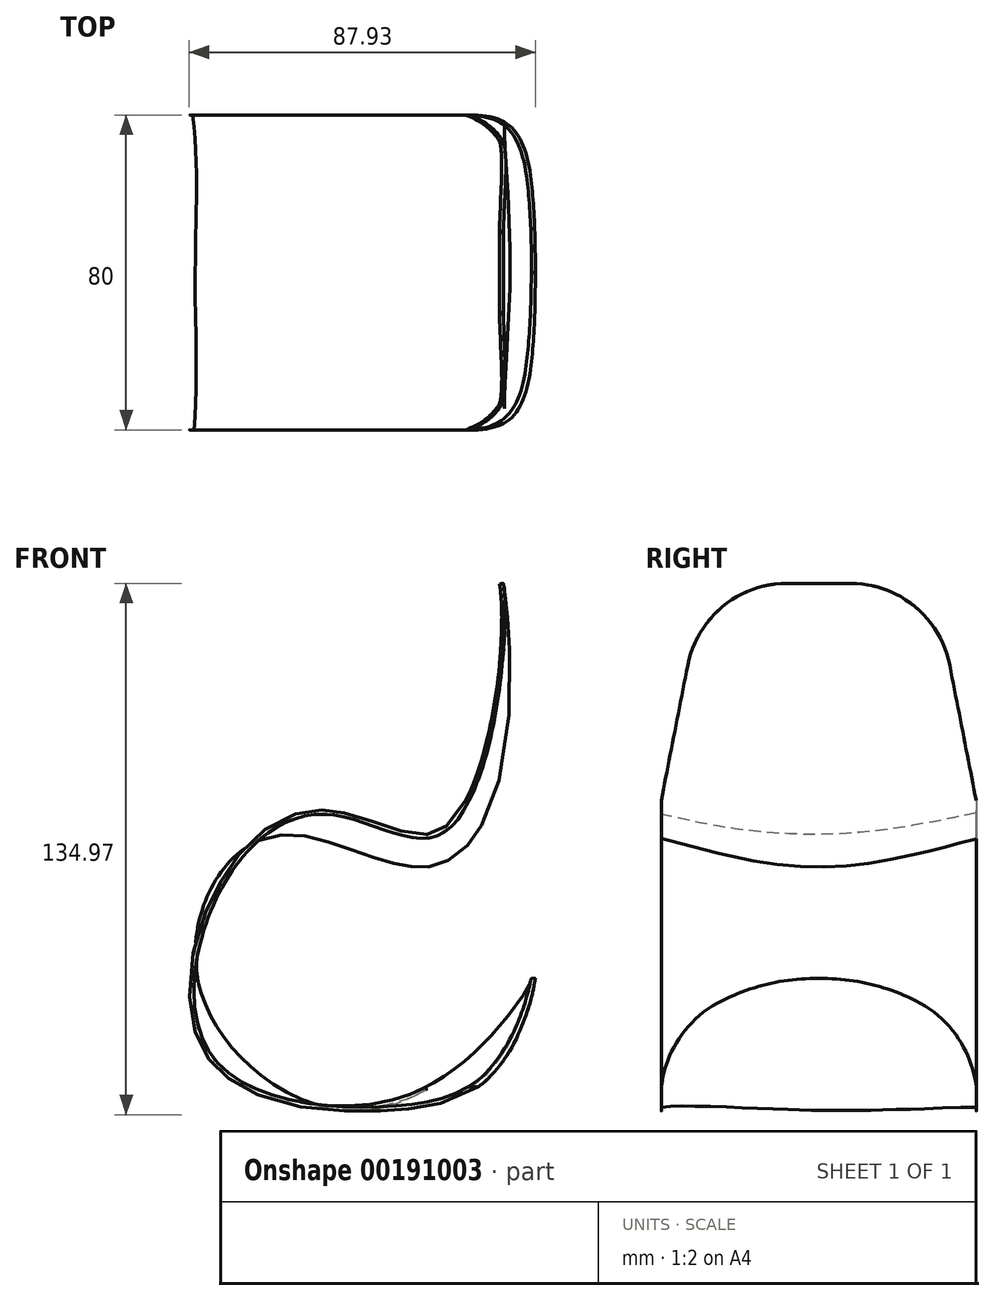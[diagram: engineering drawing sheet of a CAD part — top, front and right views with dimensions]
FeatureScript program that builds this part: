
annotation { "Feature Type Name" : "Feature", "Feature Type Description" : "" }
export const myFeature = defineFeature(function(context is Context, id is Id, definition is map)
    precondition{}
    {
        {
            var Q0;
            Q0=qCreatedBy(makeId("Front.planeOp"),FACE);
            cPlane(context, id + "F0", {"entities" : qUnion([Q0]), "cplaneType" : CPlaneType.OFFSET, "offset" : 40 * mm, "width" : 150 * mm, "height" : 150 * mm});
        }
        {
            var Q0;
            Q0=qCreatedBy(id+"F0.planeOp",FACE);
            var sketch = newSketch(context, id + "F1", { "sketchPlane" : qUnion([Q0])});
            skFitSpline(sketch, "E0", {"points": [v(44.76, 63.94) * mm, v(27.54, 0) * mm, v(0, 5.5) * mm, v(-26.55, -12.21) * mm, v(-29.21, -56.35) * mm, v(18.08, -68.48) * mm, v(50.82, -42.77) * mm], "startDerivative": vector(-17.73, -450.31) * mm, "endDerivative": vector(137.22, 364.15) * mm});
            skFitSpline(sketch, "E1.0", {"points": [v(43.76, 63.98) * mm, v(43.4, 54.62) * mm, v(42.39, 40.95) * mm, v(39.87, 25.25) * mm, v(37.32, 15.2) * mm, v(34.6, 8.64) * mm, v(32.1, 4.74) * mm, v(30.05, 2.54) * mm, v(28.24, 1.33) * mm, v(26.73, 0.75) * mm, v(25.12, 0.4) * mm, v(22.94, 0.35) * mm, v(20.06, 0.82) * mm, v(16.97, 1.69) * mm, v(13.73, 2.8) * mm, v(10.37, 4.02) * mm, v(6.93, 5.16) * mm, v(4.01, 5.93) * mm, v(1.67, 6.34) * mm, v(-0.1, 6.53) * mm, v(-1.86, 6.57) * mm, v(-4.18, 6.44) * mm, v(-7.03, 5.94) * mm, v(-10.35, 4.82) * mm, v(-14.61, 2.7) * mm, v(-18.59, -0.35) * mm, v(-22.21, -4.17) * mm, v(-24.74, -7.4) * mm, v(-27.06, -10.98) * mm, v(-29.16, -14.88) * mm, v(-31, -19.03) * mm, v(-33.08, -24.82) * mm, v(-34.87, -32.36) * mm, v(-35.35, -39.87) * mm, v(-34.78, -45.59) * mm, v(-33.84, -49.66) * mm, v(-32.33, -53.46) * mm, v(-30.57, -56.32) * mm, v(-28.85, -58.4) * mm, v(-26.93, -60.3) * mm, v(-24.2, -62.4) * mm, v(-20.47, -64.5) * mm, v(-15.02, -66.76) * mm, v(-7.48, -68.71) * mm, v(0.53, -69.66) * mm, v(6.92, -69.92) * mm, v(11.63, -69.9) * mm, v(15.43, -69.7) * mm, v(18.36, -69.47) * mm, v(21.2, -69.17) * mm, v(24.6, -68.68) * mm, v(29.73, -67.53) * mm, v(35.62, -65.24) * mm, v(41.84, -60.56) * mm, v(47.22, -53.53) * mm, v(50.31, -46.96) * mm, v(51.76, -43.12) * mm]});
            skLineSegment(sketch, "E2", {"start": v(43.76, 63.98) * mm, "end": v(44.76, 63.94) * mm});
            skLineSegment(sketch, "E3", {"start": v(50.82, -42.77) * mm, "end": v(51.76, -43.12) * mm});
            skSolve(sketch);
        }
        {
            var Q0;
            Q0=qCreatedBy(makeId("Front.planeOp"),FACE);
            var sketch = newSketch(context, id + "F2", { "sketchPlane" : qUnion([Q0])});
            skFitSpline(sketch, "E4", {"points": [v(44.43, 64.18) * mm, v(26.14, -7.7) * mm, v(-14.33, 0) * mm, v(-33.1, -36.83) * mm, v(12.22, -69.2) * mm, v(50.9, -38.12) * mm, v(51.56, -35.53) * mm], "startDerivative": vector(72.36, -532.06) * mm, "endDerivative": vector(-2.03, 40.07) * mm});
            skFitSpline(sketch, "E5.0", {"points": [v(43.44, 64.05) * mm, v(44.94, 53.01) * mm, v(45.68, 37.82) * mm, v(44, 21.13) * mm, v(41.53, 10.63) * mm, v(38.53, 3.74) * mm, v(35.65, -0.55) * mm, v(33.27, -3.13) * mm, v(30.7, -5.06) * mm, v(28.4, -6.12) * mm, v(26.45, -6.64) * mm, v(24.44, -6.94) * mm, v(21.76, -6.92) * mm, v(18.32, -6.37) * mm, v(13.5, -5.1) * mm, v(8.4, -3.27) * mm, v(3.2, -1.43) * mm, v(-0.73, -0.17) * mm, v(-4.65, 0.82) * mm, v(-7.9, 1.3) * mm, v(-10.45, 1.41) * mm, v(-12.35, 1.33) * mm, v(-14.23, 1.07) * mm, v(-16.07, 0.61) * mm, v(-17.86, -0.03) * mm, v(-20.16, -1.14) * mm, v(-22.87, -2.94) * mm, v(-25.82, -5.68) * mm, v(-29.3, -10) * mm, v(-32.7, -16.45) * mm, v(-34.55, -23.81) * mm, v(-34.93, -29.95) * mm, v(-34.67, -33.83) * mm, v(-34.13, -36.92) * mm, v(-33.38, -39.99) * mm, v(-32.03, -43.74) * mm, v(-29.84, -48.08) * mm, v(-26.23, -53.57) * mm, v(-20.56, -59.74) * mm, v(-13.73, -64.65) * mm, v(-7.8, -67.61) * mm, v(-3.16, -69.3) * mm, v(1.6, -70.37) * mm, v(6.45, -70.79) * mm, v(10.5, -70.54) * mm, v(13.7, -69.95) * mm, v(16.88, -69.11) * mm, v(20.76, -67.64) * mm, v(25.26, -65.31) * mm, v(29.54, -62.55) * mm, v(34.93, -58.44) * mm, v(39.75, -53.94) * mm, v(43.85, -49.5) * mm, v(46.51, -46.33) * mm, v(48.74, -43.43) * mm, v(50.19, -41.32) * mm, v(51.09, -39.88) * mm, v(51.63, -38.92) * mm, v(52.04, -38.1) * mm, v(52.31, -37.42) * mm, v(52.48, -36.81) * mm, v(52.56, -36.28) * mm, v(52.57, -35.82) * mm, v(52.56, -35.58) * mm, v(52.55, -35.48) * mm]});
            skLineSegment(sketch, "E6", {"start": v(43.44, 64.05) * mm, "end": v(44.43, 64.18) * mm});
            skLineSegment(sketch, "E7", {"start": v(51.56, -35.53) * mm, "end": v(52.55, -35.48) * mm});
            skSolve(sketch);
        }
        {
            var Q0;
            Q0=qCreatedBy(makeId("Front.planeOp"),FACE);
            cPlane(context, id + "F3", {"entities" : qUnion([Q0]), "cplaneType" : CPlaneType.OFFSET, "offset" : 40 * mm, "oppositeDirection" : true, "width" : 150 * mm, "height" : 150 * mm});
        }
        {
            var Q0;
            Q0=qCreatedBy(id+"F3.planeOp",FACE);
            var sketch = newSketch(context, id + "F4", { "sketchPlane" : qUnion([Q0])});
            skFitSpline(sketch, "E8.0", {"points": [v(43.76, 63.98) * mm, v(43.4, 54.62) * mm, v(42.39, 40.95) * mm, v(39.87, 25.25) * mm, v(37.32, 15.2) * mm, v(34.6, 8.64) * mm, v(32.1, 4.74) * mm, v(30.05, 2.54) * mm, v(28.24, 1.33) * mm, v(26.73, 0.75) * mm, v(25.12, 0.4) * mm, v(22.94, 0.35) * mm, v(20.06, 0.82) * mm, v(16.97, 1.69) * mm, v(13.73, 2.8) * mm, v(10.37, 4.02) * mm, v(6.93, 5.16) * mm, v(4.01, 5.93) * mm, v(1.67, 6.34) * mm, v(-0.1, 6.53) * mm, v(-1.86, 6.57) * mm, v(-4.18, 6.44) * mm, v(-7.03, 5.94) * mm, v(-10.35, 4.82) * mm, v(-14.61, 2.7) * mm, v(-18.59, -0.35) * mm, v(-22.21, -4.17) * mm, v(-24.74, -7.4) * mm, v(-27.06, -10.98) * mm, v(-29.16, -14.88) * mm, v(-31, -19.03) * mm, v(-33.08, -24.82) * mm, v(-34.87, -32.36) * mm, v(-35.35, -39.87) * mm, v(-34.78, -45.59) * mm, v(-33.84, -49.66) * mm, v(-32.33, -53.46) * mm, v(-30.57, -56.32) * mm, v(-28.85, -58.4) * mm, v(-26.93, -60.3) * mm, v(-24.2, -62.4) * mm, v(-20.47, -64.5) * mm, v(-15.02, -66.76) * mm, v(-7.48, -68.71) * mm, v(0.53, -69.66) * mm, v(6.92, -69.92) * mm, v(11.63, -69.9) * mm, v(15.43, -69.7) * mm, v(18.36, -69.47) * mm, v(21.2, -69.17) * mm, v(24.6, -68.68) * mm, v(29.73, -67.53) * mm, v(35.62, -65.24) * mm, v(41.84, -60.56) * mm, v(47.22, -53.53) * mm, v(50.31, -46.96) * mm, v(51.76, -43.12) * mm]});
            skFitSpline(sketch, "E9.0", {"points": [v(44.76, 63.94) * mm, v(44.57, 59.25) * mm, v(44.05, 50) * mm, v(42.75, 36.9) * mm, v(40.85, 25.06) * mm, v(38.7, 16.59) * mm, v(36.62, 10.88) * mm, v(34.86, 7.19) * mm, v(32.9, 4.14) * mm, v(30.72, 1.78) * mm, v(28.72, 0.45) * mm, v(27.01, -0.21) * mm, v(25.22, -0.6) * mm, v(22.85, -0.65) * mm, v(19.83, -0.16) * mm, v(16.67, 0.74) * mm, v(12.3, 2.24) * mm, v(6.64, 4.33) * mm, v(-0.2, 5.87) * mm, v(-6.83, 5.21) * mm, v(-13.1, 2.58) * mm, v(-17.92, -1.1) * mm, v(-21.45, -4.82) * mm, v(-23.92, -7.99) * mm, v(-26.2, -11.5) * mm, v(-28.26, -15.32) * mm, v(-30.07, -19.4) * mm, v(-32.12, -25.1) * mm, v(-33.88, -32.52) * mm, v(-34.43, -41.34) * mm, v(-33.14, -49.52) * mm, v(-29.72, -56.51) * mm, v(-23.87, -61.75) * mm, v(-16.2, -65.42) * mm, v(-7.3, -67.73) * mm, v(0.6, -68.66) * mm, v(6.94, -68.92) * mm, v(11.6, -68.9) * mm, v(15.37, -68.7) * mm, v(18.26, -68.47) * mm, v(21.07, -68.18) * mm, v(24.42, -67.7) * mm, v(28.18, -66.85) * mm, v(31.72, -65.68) * mm, v(36.13, -63.6) * mm, v(41.12, -59.86) * mm, v(46.34, -53.03) * mm, v(49.4, -46.56) * mm, v(50.82, -42.77) * mm]});
            skLineSegment(sketch, "E10", {"start": v(43.76, 63.98) * mm, "end": v(44.76, 63.94) * mm});
            skLineSegment(sketch, "E11", {"start": v(50.82, -42.77) * mm, "end": v(51.76, -43.12) * mm});
            skSolve(sketch);
        }
        {
            var Q0;
            Q0 = qSketchRegion(id + "F1", true);
            var Q1;
            Q1 = qSketchRegion(id + "F2", true);
            var Q2;
            Q2 = qSketchRegion(id + "F4", true);
            loft(context, id + "F5", {"sheetProfilesArray" : [{ "sheetProfileEntities" : qUnion([Q0]) }, { "sheetProfileEntities" : qUnion([Q1]) }, { "sheetProfileEntities" : qUnion([Q2]) }]});
        }
        {
            var Q0;
            Q0=qCreatedBy(makeId("Right.planeOp"),FACE);
            var sketch = newSketch(context, id + "F6", { "sketchPlane" : qUnion([Q0])});
            skLineSegment(sketch, "E12", {"start": v(33.28, 43.4) * mm, "end": v(40.27, 7.72) * mm});
            skLineSegment(sketch, "E13", {"start": v(40.27, 7.72) * mm, "end": v(50.1, 8.9) * mm});
            skLineSegment(sketch, "E14", {"start": v(50.1, 8.9) * mm, "end": v(47.4, 68.54) * mm});
            skLineSegment(sketch, "E15", {"start": v(47.4, 68.54) * mm, "end": v(0, 70.38) * mm});
            skLineSegment(sketch, "E16.MirrorCS", {"start": v(-47.4, 68.54) * mm, "end": v(0, 70.38) * mm});
            skLineSegment(sketch, "E17.MirrorCS", {"start": v(-50.1, 8.9) * mm, "end": v(-47.4, 68.54) * mm});
            skLineSegment(sketch, "E18.MirrorCS", {"start": v(-40.27, 7.72) * mm, "end": v(-50.1, 8.9) * mm});
            skLineSegment(sketch, "E19", {"start": v(0, 64.21) * mm, "end": v(8, 64.21) * mm});
            skArc(sketch, "E20", {"start": v(33.28, 43.4) * mm, "mid": v(24.37, 58.34) * mm, "end": v(8, 64.21) * mm});
            skLineSegment(sketch, "E21.MirrorCS", {"start": v(0, 64.21) * mm, "end": v(-8, 64.21) * mm});
            skArc(sketch, "E22.MirrorCS", {"start": v(-33.28, 43.4) * mm, "mid": v(-24.37, 58.34) * mm, "end": v(-8, 64.21) * mm});
            skLineSegment(sketch, "E23", {"start": v(-33.28, 43.4) * mm, "end": v(-40.27, 7.72) * mm});
            skSolve(sketch);
        }
        {
            var Q0;
            Q0 = qSketchRegion(id + "F6", true);
            extrude(context, id + "F7", {"entities" : qUnion([Q0]), "operationType" : NewBodyOperationType.REMOVE, "endBound" : BoundingType.THROUGH_ALL, "depth" : 25 * mm});
        }
        {
            var Q0;
            Q0=qCreatedBy(makeId("Right.planeOp"),FACE);
            var sketch = newSketch(context, id + "F8", { "sketchPlane" : qUnion([Q0])});
            skLineSegment(sketch, "E24", {"start": v(-63.09, -35.2) * mm, "end": v(51.03, -27.75) * mm});
            skLineSegment(sketch, "E25", {"start": v(51.03, -27.75) * mm, "end": v(51.41, -50.5) * mm});
            skArc(sketch, "E26", {"start": v(0, -36.2) * mm, "mid": v(-12.65, -37.53) * mm, "end": v(-24.63, -41.83) * mm});
            skArc(sketch, "E27", {"start": v(-24.63, -41.83) * mm, "mid": v(-38.84, -58.42) * mm, "end": v(-36.93, -80.18) * mm});
            skArc(sketch, "E28.MirrorCS", {"start": v(0, -36.2) * mm, "mid": v(12.65, -37.53) * mm, "end": v(24.63, -41.83) * mm});
            skArc(sketch, "E29.MirrorCS", {"start": v(24.63, -41.83) * mm, "mid": v(38.84, -58.42) * mm, "end": v(36.93, -80.18) * mm});
            skLineSegment(sketch, "E30", {"start": v(36.93, -80.18) * mm, "end": v(51.96, -77.05) * mm});
            skLineSegment(sketch, "E31", {"start": v(51.96, -77.05) * mm, "end": v(51.41, -50.5) * mm});
            skLineSegment(sketch, "E32", {"start": v(-63.09, -35.2) * mm, "end": v(-56.26, -72.15) * mm});
            skLineSegment(sketch, "E33", {"start": v(-56.26, -72.15) * mm, "end": v(-36.93, -80.18) * mm});
            skSolve(sketch);
        }
        {
            var Q0;
            Q0=makeQuery(id+"F8.imprint","IMPRINT",FACE,{"disambiguationData":[TD([[makeQuery(id+"F8.imprint","IMPRINT",EDGE,{"derivedFrom":sQuery(id+"F8.wireOp",EDGE,"E24")}),-1.0]])]});
            extrude(context, id + "F9", {"entities" : qUnion([Q0]), "operationType" : NewBodyOperationType.REMOVE, "endBound" : BoundingType.THROUGH_ALL, "depth" : 25 * mm});
        }
    });
